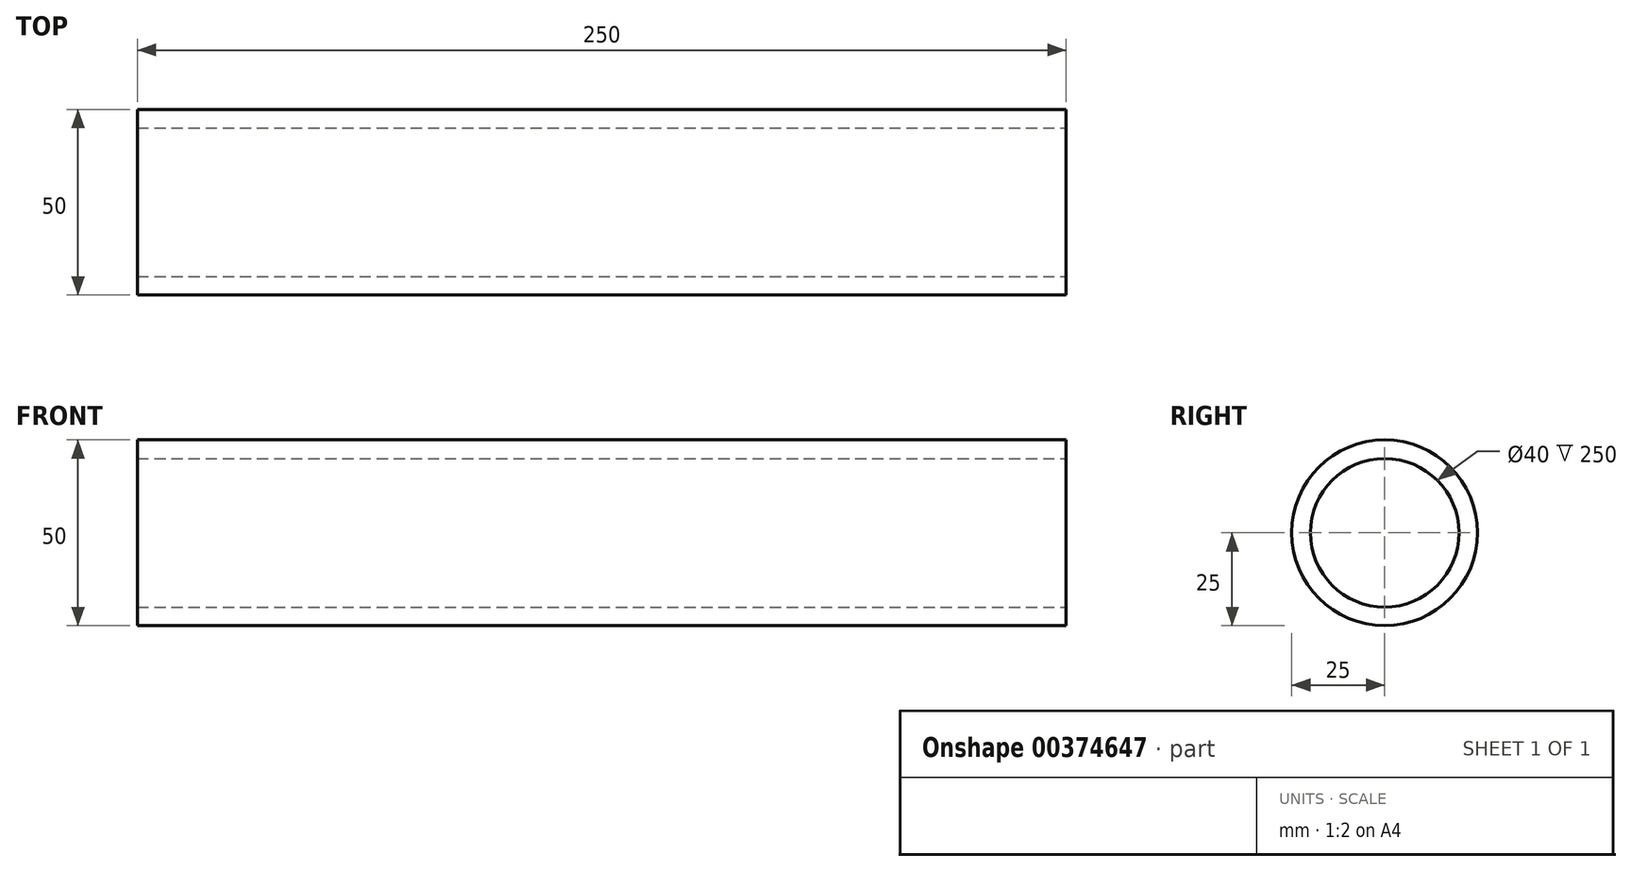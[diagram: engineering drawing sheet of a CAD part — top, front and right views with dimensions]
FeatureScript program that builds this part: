
annotation { "Feature Type Name" : "Feature", "Feature Type Description" : "" }
export const myFeature = defineFeature(function(context is Context, id is Id, definition is map)
    precondition{}
    {
        {
            var Q0;
            Q0=qCreatedBy(makeId("Front.planeOp"),FACE);
            var sketch = newSketch(context, id + "F0", { "sketchPlane" : qUnion([Q0])});
            skLineSegment(sketch, "E0.bottom", {"start": v(0, 0) * mm, "end": v(0, 0) * mm});
            skLineSegment(sketch, "E0.top", {"start": v(0, 5) * mm, "end": v(250, 5) * mm});
            skLineSegment(sketch, "E0.left", {"start": v(0, 0) * mm, "end": v(0, 5) * mm});
            skPoint(sketch, "E1.left.start.orphan", {"position": v(0, 0) * mm});
            skLineSegment(sketch, "E2", {"start": v(352.01, -20) * mm, "end": v(-116.71, -20) * mm, "construction": true});
            skLineSegment(sketch, "E3", {"start": v(0, 0) * mm, "end": v(250, 0) * mm});
            skLineSegment(sketch, "E4", {"start": v(250, 0) * mm, "end": v(250, 5) * mm});
            skSolve(sketch);
        }
        {
            var Q0;
            Q0=makeQuery(id+"F0.imprint","IMPRINT",FACE,{"disambiguationData":[TD([[makeQuery(id+"F0.imprint","IMPRINT",EDGE,{"derivedFrom":sQuery(id+"F0.wireOp",EDGE,"E0.top")}),-1.0]])]});
            var Q1;
            Q1=sQuery(id+"F0.wireOp",EDGE,"E2");
            revolve(context, id + "F1", {"entities" : qUnion([Q0]), "axis" : qUnion([Q1]), "revolveType" : RevolveType.FULL});
        }
    });
